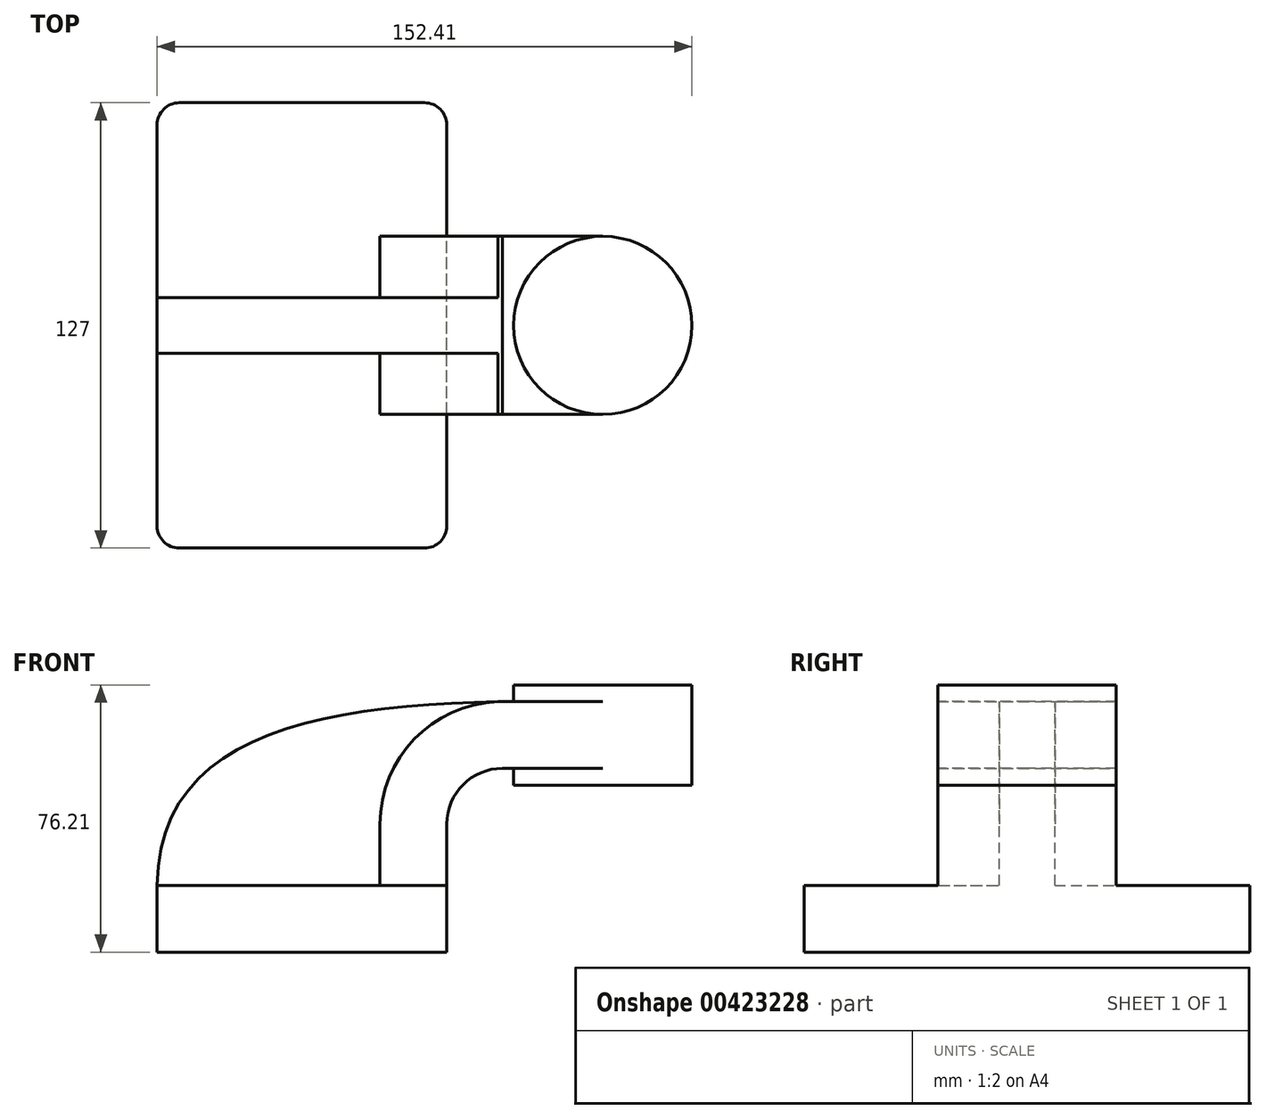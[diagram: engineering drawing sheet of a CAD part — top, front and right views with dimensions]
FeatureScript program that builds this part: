
annotation { "Feature Type Name" : "Feature", "Feature Type Description" : "" }
export const myFeature = defineFeature(function(context is Context, id is Id, definition is map)
    precondition{}
    {
        {
            var Q0;
            Q0=qCreatedBy(makeId("Front.planeOp"),FACE);
            var sketch = newSketch(context, id + "F0", { "sketchPlane" : qUnion([Q0])});
            skLineSegment(sketch, "E0.bottom", {"start": v(-41.28, -9.53) * mm, "end": v(41.28, -9.53) * mm});
            skLineSegment(sketch, "E0.top", {"start": v(-41.28, 9.52) * mm, "end": v(41.27, 9.52) * mm});
            skLineSegment(sketch, "E0.left", {"start": v(-41.27, -9.53) * mm, "end": v(-41.28, 9.52) * mm});
            skLineSegment(sketch, "E0.right", {"start": v(41.28, -9.53) * mm, "end": v(41.27, 9.52) * mm});
            skPoint(sketch, "E0.middle", {"position": v(0, 0) * mm});
            skLineSegment(sketch, "E1.bottom", {"start": v(60.32, 38.1) * mm, "end": v(111.12, 38.1) * mm});
            skLineSegment(sketch, "E1.top", {"start": v(60.32, 66.67) * mm, "end": v(111.12, 66.67) * mm});
            skLineSegment(sketch, "E1.left", {"start": v(60.32, 38.1) * mm, "end": v(60.32, 66.67) * mm});
            skLineSegment(sketch, "E1.right", {"start": v(111.12, 38.1) * mm, "end": v(111.12, 66.67) * mm});
            skPoint(sketch, "E1.middle", {"position": v(85.72, 52.39) * mm});
            skLineSegment(sketch, "E2", {"start": v(41.27, 9.52) * mm, "end": v(41.27, 27) * mm});
            skArc(sketch, "E3", {"start": v(41.27, 27) * mm, "mid": v(45.92, 38.23) * mm, "end": v(57.15, 42.88) * mm});
            skLineSegment(sketch, "E4", {"start": v(57.15, 42.88) * mm, "end": v(85.73, 42.88) * mm});
            skLineSegment(sketch, "E5.0", {"start": v(57.15, 61.93) * mm, "end": v(85.73, 61.93) * mm});
            skArc(sketch, "E5.1", {"start": v(22.22, 27) * mm, "mid": v(32.45, 51.7) * mm, "end": v(57.15, 61.93) * mm});
            skLineSegment(sketch, "E5.2", {"start": v(22.22, 9.52) * mm, "end": v(22.22, 27) * mm});
            skLineSegment(sketch, "E6", {"start": v(85.73, 42.88) * mm, "end": v(85.73, 61.93) * mm});
            skFitSpline(sketch, "E7", {"points": [v(-41.28, 9.53) * mm, v(57.15, 61.93) * mm], "startDerivative": vector(1.07, 130.06) * mm, "endDerivative": vector(155.16, 2.77) * mm});
            skLineSegment(sketch, "E8", {"start": v(85.72, 38.1) * mm, "end": v(85.72, 66.67) * mm});
            skSolve(sketch);
        }
        {
            var Q0;
            Q0=makeQuery(id+"F0.imprint","IMPRINT",FACE,{"disambiguationData":[TD([[makeQuery(id+"F0.imprint","IMPRINT",EDGE,{"derivedFrom":sQuery(id+"F0.wireOp",EDGE,"E0.bottom")}),1.0]])]});
            extrude(context, id + "F1", {"entities" : qUnion([Q0]), "endBound" : BoundingType.SYMMETRIC, "depth" : 127 * mm});
        }
        {
            var Q0;
            {var subQ0=sQuery(id+"F0.wireOp",EDGE,"E2");Q0=makeQuery(id+"F0.imprint","IMPRINT",FACE,{"disambiguationData":[TD([[makeQuery(id+"F0.imprint","IMPRINT",EDGE,{"derivedFrom":subQ0}),1.0]])]});}
            var Q1;
            {var subQ5=sQuery(id+"F0.wireOp",EDGE,"E6");Q1=makeQuery(id+"F0.imprint","IMPRINT",FACE,{"disambiguationData":[TD([[makeQuery(id+"F0.imprint","IMPRINT",EDGE,{"derivedFrom":subQ5}),1.0]])]});}
            extrude(context, id + "F2", {"entities" : qUnion([Q0, Q1]), "operationType" : NewBodyOperationType.ADD, "endBound" : BoundingType.SYMMETRIC, "depth" : 50.8 * mm});
        }
        {
            var Q0;
            {var subQ3=sQuery(id+"F0.wireOp",EDGE,"E5.2");Q0=makeQuery(id+"F0.imprint","IMPRINT",FACE,{"disambiguationData":[TD([[makeQuery(id+"F0.imprint","IMPRINT",EDGE,{"derivedFrom":subQ3}),1.0]])]});}
            extrude(context, id + "F3", {"entities" : qUnion([Q0]), "operationType" : NewBodyOperationType.ADD, "endBound" : BoundingType.SYMMETRIC, "depth" : 15.88 * mm});
        }
        {
            var Q0;
            {var subQ0=sQuery(id+"F0.wireOp",EDGE,"E4");var subQ1=sQuery(id+"F0.wireOp",EDGE,"E1.left");var subQ2=makeQuery(id+"F0.imprint","INTERSECT",VERTEX,{"derivedFrom":[subQ1,subQ0]});Q0=makeQuery(id+"F0.imprint","IMPRINT",FACE,{"disambiguationData":[TD([[makeQuery(id+"F0.imprint","IMPRINT",EDGE,{"disambiguationData":[TD([[subQ2,-1.0]])],"derivedFrom":subQ1}),-1.0]])]});}
            extrude(context, id + "F4", {"entities" : qUnion([Q0]), "operationType" : NewBodyOperationType.ADD, "endBound" : BoundingType.SYMMETRIC, "depth" : 50.8 * mm});
        }
        {
            var Q0;
            {var subQ4=sQuery(id+"F0.wireOp",EDGE,"E1.right");Q0=makeQuery(id+"F0.imprint","IMPRINT",FACE,{"disambiguationData":[TD([[makeQuery(id+"F0.imprint","IMPRINT",EDGE,{"derivedFrom":subQ4}),1.0]])]});}
            var Q1;
            Q1=sQuery(id+"F0.wireOp",EDGE,"E8");
            revolve(context, id + "F5", {"operationType" : NewBodyOperationType.ADD, "entities" : qUnion([Q0]), "axis" : qUnion([Q1]), "revolveType" : RevolveType.FULL});
        }
        {
            var Q0;
            Q0=makeQuery(id+"F1.opExtrude","CAP_EDGE",EDGE,{"disambiguationData":[OSD([sQuery(id+"F0.wireOp",EDGE,"E0.right")])],"isStart":false});
            var Q1;
            Q1=makeQuery(id+"F1.opExtrude","CAP_EDGE",EDGE,{"disambiguationData":[OSD([sQuery(id+"F0.wireOp",EDGE,"E0.left")])],"isStart":true});
            var Q2;
            Q2=makeQuery(id+"F1.opExtrude","CAP_EDGE",EDGE,{"disambiguationData":[OSD([sQuery(id+"F0.wireOp",EDGE,"E0.left")])],"isStart":false});
            var Q3;
            Q3=makeQuery(id+"F1.opExtrude","CAP_EDGE",EDGE,{"disambiguationData":[OSD([sQuery(id+"F0.wireOp",EDGE,"E0.right")])],"isStart":true});
            fillet(context, id + "F6", {"entities" : qUnion([Q0, Q1, Q2, Q3]), "radius" : 6.35 * mm, "tangentPropagation" : true, "allowEdgeOverflow" : false});
        }
    });
